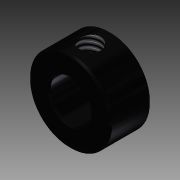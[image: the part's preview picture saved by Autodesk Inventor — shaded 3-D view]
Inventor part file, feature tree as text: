
AUTODESK INVENTOR PART (.ipt)
format: ipt  version: 2014 (Build 180170000, 170)  size: 116,224 bytes
history: native  units: in
note: dims shown in document units (in); Inventor stores cm internally (conversion verified against a paired STEP export)
features: sketch x3, extrude x2, chamfer x1, plane x1, hole x1
ambient origin geometry x8: Origin, YZ Plane, XZ Plane, XY Plane, X Axis, Y Axis, Z Axis, Center Point
bodies: Solid1 (feature_tree)
feature tree (8):
  extrude  "Extrusion1"  Depth=0.375in TaperAngle=0.0deg
  extrude  "Extrusion2"  Depth=0.375in TaperAngle=0.0deg
  chamfer  "Chamfer1"  Distance=0.0156in Angle=45.0deg
  plane  "Work Plane1"
  hole  "Hole1"  [1 undecoded]
  sketch  "Sketch1"  dims[d0=0.75in d1=0.375in d2=0.0in]
  sketch  "Sketch2"  dims[d3=0.375in d4=0.281in d5=0.0in d6=0.0156in d7=0.125in d8=45.0deg]
  sketch  "Sketch3"  dims[d9=0.196in d10=0.75in d11=0.375in d12=0.25in d13=0.5635in d14=1.0in d15=0.8108in]
note: 1 required parameter value undecoded (feature->parameter linkage not recoverable at this tier; creation-order binding heuristic only, values carry confidence <= 0.55)
